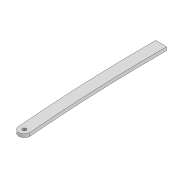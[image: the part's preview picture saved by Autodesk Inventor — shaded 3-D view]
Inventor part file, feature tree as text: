
AUTODESK INVENTOR PART (.ipt)
format: ipt  version: 2022 (Build 260153000, 153)  size: 100,864 bytes
history: native  units: mm
features: extrude x2, sketch x2
ambient origin geometry x8: Origin, YZ Plane, XZ Plane, XY Plane, X Axis, Y Axis, Z Axis, Center Point
bodies: Solid1 (feature_tree)
feature tree (4):
  extrude  "Extrusion1"  Depth=3.3mm
  extrude  "Extrusion2"  Depth=10.0mm
  sketch  "Sketch1"  dims[d0=3.3mm d1=3.3mm]
  sketch  "Sketch2"  dims[d2=10.0mm d3=253.429mm d6=3.0mm d7=0.0mm d16=1500.0mm d17=1500.0mm d18=10.0mm d19=0.0mm]
